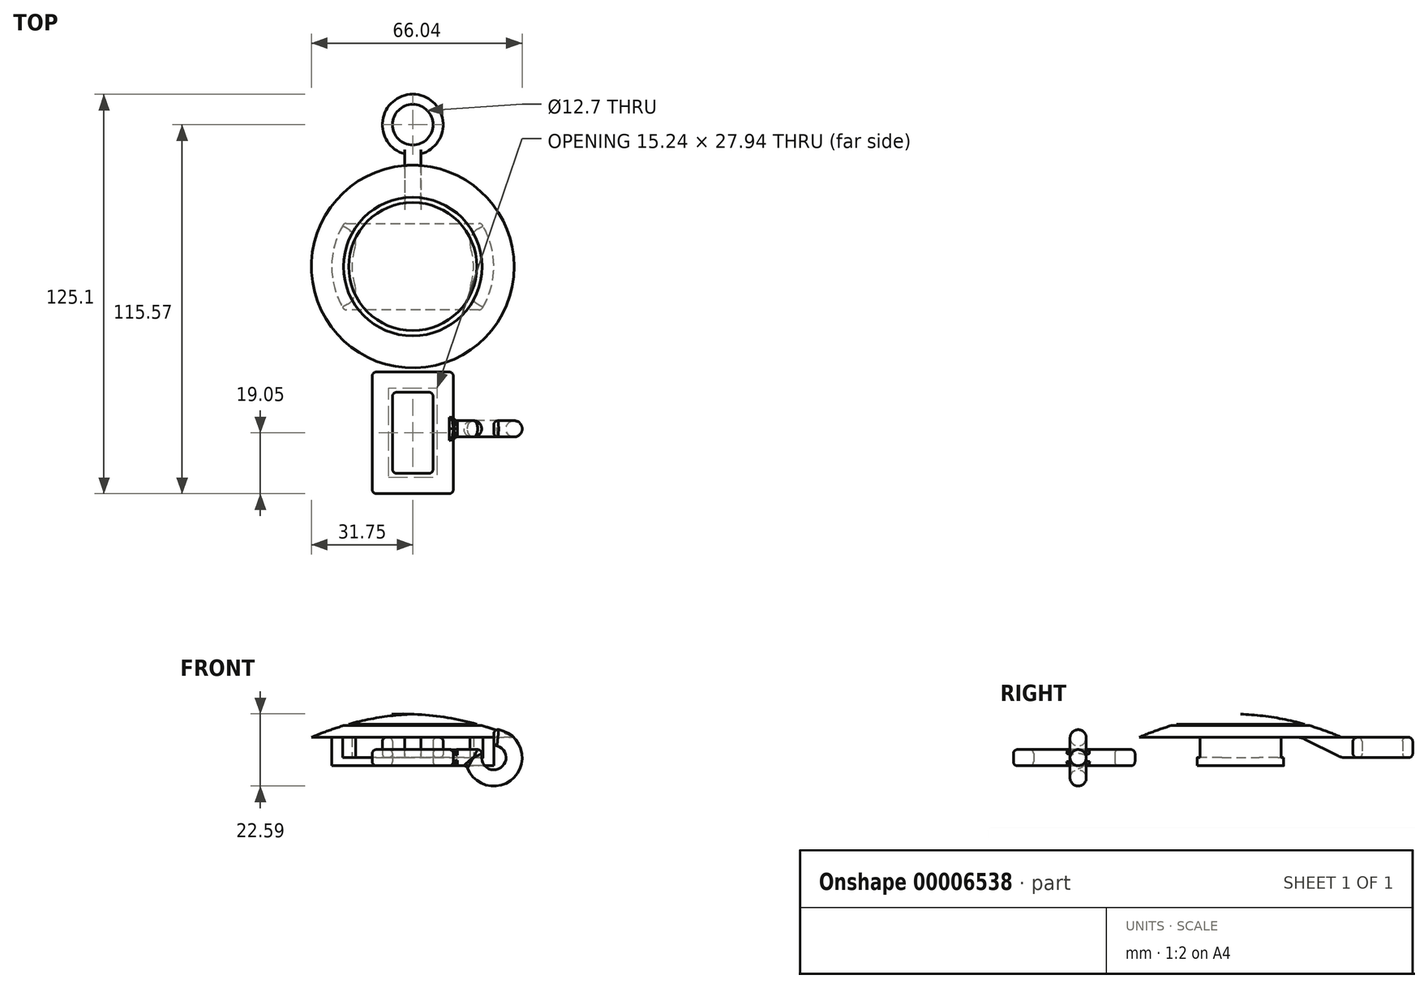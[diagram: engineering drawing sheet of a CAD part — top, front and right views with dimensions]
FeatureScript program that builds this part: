
annotation { "Feature Type Name" : "Feature", "Feature Type Description" : "" }
export const myFeature = defineFeature(function(context is Context, id is Id, definition is map)
    precondition{}
    {
        {
            var Q0;
            Q0=qCreatedBy(makeId("Top.planeOp"),FACE);
            var sketch = newSketch(context, id + "F0", { "sketchPlane" : qUnion([Q0])});
            skArc(sketch, "E0", {"start": v(-21.5, 13.54) * mm, "mid": v(-25.4, 0) * mm, "end": v(-21.5, -13.54) * mm});
            skLineSegment(sketch, "E1", {"start": v(-21.5, 13.54) * mm, "end": v(21.5, 13.54) * mm});
            skLineSegment(sketch, "E2", {"start": v(21.5, -13.54) * mm, "end": v(-21.5, -13.54) * mm});
            skArc(sketch, "E3.trimOffspring", {"start": v(21.5, -13.54) * mm, "mid": v(25.4, 0) * mm, "end": v(21.5, 13.54) * mm});
            skSolve(sketch);
        }
        {
            var Q0;
            Q0=makeQuery(id+"F0.imprint","IMPRINT",FACE,{"disambiguationData":[TD([[makeQuery(id+"F0.imprint","IMPRINT",EDGE,{"derivedFrom":sQuery(id+"F0.wireOp",EDGE,"E0")}),1.0]])]});
            extrude(context, id + "F1", {"entities" : qUnion([Q0]), "oppositeDirection" : true, "depth" : 2.54 * mm});
        }
        {
            var Q0;
            Q0=qCreatedBy(makeId("Top.planeOp"),FACE);
            var sketch = newSketch(context, id + "F2", { "sketchPlane" : qUnion([Q0])});
            skArc(sketch, "E4", {"start": v(-16.5, 9.52) * mm, "mid": v(-19.05, 0) * mm, "end": v(-16.5, -9.53) * mm});
            skArc(sketch, "E5", {"start": v(-22, 12.7) * mm, "mid": v(-25.4, 0) * mm, "end": v(-22, -12.7) * mm});
            skLineSegment(sketch, "E6", {"start": v(19.05, 0) * mm, "end": v(37.65, 0) * mm});
            skLineSegment(sketch, "E7", {"start": v(16.5, 9.53) * mm, "end": v(22, 12.7) * mm});
            skLineSegment(sketch, "E8", {"start": v(16.5, -9.53) * mm, "end": v(22, -12.7) * mm});
            skLineSegment(sketch, "E9", {"start": v(-16.5, -9.53) * mm, "end": v(-22, -12.7) * mm});
            skLineSegment(sketch, "E10", {"start": v(-19.05, 0) * mm, "end": v(-25.4, 0) * mm});
            skLineSegment(sketch, "E11", {"start": v(-16.5, 9.53) * mm, "end": v(-22, 12.7) * mm});
            skArc(sketch, "E12.trimOffspring", {"start": v(16.5, -9.53) * mm, "mid": v(19.05, 0) * mm, "end": v(16.5, 9.53) * mm});
            skArc(sketch, "E13.trimOffspring", {"start": v(22, -12.7) * mm, "mid": v(25.4, 0) * mm, "end": v(22, 12.7) * mm});
            skSolve(sketch);
        }
        {
            var Q0;
            {var subQ1=sQuery(id+"F2.wireOp",EDGE,"E10");Q0=makeQuery(id+"F2.imprint","IMPRINT",FACE,{"disambiguationData":[TD([[makeQuery(id+"F2.imprint","IMPRINT",EDGE,{"derivedFrom":subQ1}),-1.0]])]});}
            var Q1;
            {var subQ1=sQuery(id+"F2.wireOp",EDGE,"E9");Q1=makeQuery(id+"F2.imprint","IMPRINT",FACE,{"disambiguationData":[TD([[makeQuery(id+"F2.imprint","IMPRINT",EDGE,{"derivedFrom":subQ1}),-1.0]])]});}
            var Q2;
            {var subQ3=sQuery(id+"F2.wireOp",EDGE,"E8");Q2=makeQuery(id+"F2.imprint","IMPRINT",FACE,{"disambiguationData":[TD([[makeQuery(id+"F2.imprint","IMPRINT",EDGE,{"derivedFrom":subQ3}),1.0]])]});}
            var Q3;
            {var subQ3=sQuery(id+"F2.wireOp",EDGE,"E7");Q3=makeQuery(id+"F2.imprint","IMPRINT",FACE,{"disambiguationData":[TD([[makeQuery(id+"F2.imprint","IMPRINT",EDGE,{"derivedFrom":subQ3}),-1.0]])]});}
            extrude(context, id + "F3", {"entities" : qUnion([Q0, Q1, Q2, Q3]), "operationType" : NewBodyOperationType.ADD, "depth" : 6.35 * mm});
        }
        {
            var Q0;
            Q0=makeQuery(id+"F3.opExtrude","SWEPT_EDGE",EDGE,{"disambiguationData":[OSD([sQuery(id+"F2.wireOp",EDGE,"E4"),sQuery(id+"F2.wireOp",EDGE,"E9")])]});
            var Q1;
            Q1=makeQuery(id+"F3.opExtrude","SWEPT_EDGE",EDGE,{"disambiguationData":[OSD([sQuery(id+"F2.wireOp",EDGE,"E4"),sQuery(id+"F2.wireOp",EDGE,"E11")])]});
            var Q2;
            Q2=makeQuery(id+"F3.opExtrude","SWEPT_EDGE",EDGE,{"disambiguationData":[OSD([sQuery(id+"F2.wireOp",EDGE,"E8"),sQuery(id+"F2.wireOp",EDGE,"E12.trimOffspring")])]});
            var Q3;
            Q3=makeQuery(id+"F3.opExtrude","SWEPT_EDGE",EDGE,{"disambiguationData":[OSD([sQuery(id+"F2.wireOp",EDGE,"E7"),sQuery(id+"F2.wireOp",EDGE,"E12.trimOffspring")])]});
            fillet(context, id + "F4", {"entities" : qUnion([Q0, Q1, Q2, Q3]), "radius" : 5.08 * mm, "tangentPropagation" : true, "allowEdgeOverflow" : false});
        }
        {
            var Q0;
            Q0=makeQuery(id+"F1.opExtrude","SWEPT_EDGE",EDGE,{"disambiguationData":[OSD([sQuery(id+"F0.wireOp",EDGE,"E0"),sQuery(id+"F0.wireOp",EDGE,"E1")])]});
            var Q1;
            Q1=makeQuery(id+"F1.opExtrude","SWEPT_EDGE",EDGE,{"disambiguationData":[OSD([sQuery(id+"F0.wireOp",EDGE,"E1"),sQuery(id+"F0.wireOp",EDGE,"E3.trimOffspring")])]});
            var Q2;
            Q2=makeQuery(id+"F1.opExtrude","SWEPT_EDGE",EDGE,{"disambiguationData":[OSD([sQuery(id+"F0.wireOp",EDGE,"E2"),sQuery(id+"F0.wireOp",EDGE,"E3.trimOffspring")])]});
            var Q3;
            Q3=makeQuery(id+"F1.opExtrude","SWEPT_EDGE",EDGE,{"disambiguationData":[OSD([sQuery(id+"F0.wireOp",EDGE,"E0"),sQuery(id+"F0.wireOp",EDGE,"E2")])]});
            fillet(context, id + "F5", {"entities" : qUnion([Q0, Q1, Q2, Q3]), "radius" : 1.27 * mm, "tangentPropagation" : true, "allowEdgeOverflow" : false});
        }
        {
            var Q0;
            Q0=qCreatedBy(makeId("Front.planeOp"),FACE);
            var sketch = newSketch(context, id + "F6", { "sketchPlane" : qUnion([Q0])});
            skLineSegment(sketch, "E14.0", {"start": v(-25.4, 6.35) * mm, "end": v(-22, 6.35) * mm});
            skLineSegment(sketch, "E15.1", {"start": v(22, 6.35) * mm, "end": v(25.4, 6.35) * mm});
            skLineSegment(sketch, "E16", {"start": v(-25.4, 6.35) * mm, "end": v(25.4, 6.35) * mm});
            skLineSegment(sketch, "E17", {"start": v(0, 6.35) * mm, "end": v(0, 13.64) * mm});
            skPoint(sketch, "E17.endSnap0", {"position": v(0, 6.35) * mm});
            skLineSegment(sketch, "E18", {"start": v(0, 6.35) * mm, "end": v(31.75, 6.35) * mm});
            skPoint(sketch, "E18.endSnap0", {"position": v(23.7, 6.35) * mm});
            skArc(sketch, "E19", {"start": v(31.75, 6.35) * mm, "mid": v(16.22, 11.5) * mm, "end": v(0, 13.64) * mm});
            skSolve(sketch);
        }
        {
            var Q0;
            {var subQ2=sQuery(id+"F6.wireOp",EDGE,"E17");Q0=makeQuery(id+"F6.imprint","IMPRINT",FACE,{"disambiguationData":[TD([[makeQuery(id+"F6.imprint","IMPRINT",EDGE,{"derivedFrom":subQ2}),-1.0]])]});}
            var Q1;
            Q1=sQuery(id+"F6.wireOp",EDGE,"E17");
            revolve(context, id + "F7", {"operationType" : NewBodyOperationType.ADD, "entities" : qUnion([Q0]), "axis" : qUnion([Q1]), "revolveType" : RevolveType.FULL});
        }
        {
            var Q0;
            Q0=qCreatedBy(makeId("Front.planeOp"),FACE);
            var sketch = newSketch(context, id + "F8", { "sketchPlane" : qUnion([Q0])});
            skLineSegment(sketch, "E20", {"start": v(20.07, 10.74) * mm, "end": v(20.07, 10.04) * mm});
            skLineSegment(sketch, "E21", {"start": v(20.07, 10.04) * mm, "end": v(22.4, 10.04) * mm});
            skLineSegment(sketch, "E22", {"start": v(22.4, 10.04) * mm, "end": v(20.07, 10.74) * mm});
            skLineSegment(sketch, "E23", {"start": v(0, 11.08) * mm, "end": v(0, 16.1) * mm});
            skSolve(sketch);
        }
        {
            var Q0;
            Q0=makeQuery(id+"F8.imprint","IMPRINT",FACE,{"disambiguationData":[TD([[makeQuery(id+"F8.imprint","IMPRINT",EDGE,{"derivedFrom":sQuery(id+"F8.wireOp",EDGE,"E20")}),1.0]])]});
            var Q1;
            Q1=sQuery(id+"F8.wireOp",EDGE,"E23");
            revolve(context, id + "F9", {"operationType" : NewBodyOperationType.REMOVE, "entities" : qUnion([Q0]), "axis" : qUnion([Q1]), "revolveType" : RevolveType.FULL, "oppositeDirection" : true});
        }
        {
            var Q0;
            Q0=qCreatedBy(makeId("Top.planeOp"),FACE);
            var sketch = newSketch(context, id + "F10", { "sketchPlane" : qUnion([Q0])});
            skArc(sketch, "E24.1.0", {"start": v(2.54, 35.27) * mm, "mid": v(0, 53.98) * mm, "end": v(-2.54, 35.27) * mm});
            skCircle(sketch, "E24.1.1", {"center": v(0, 44.45) * mm, "radius": 6.35 * mm});
            skLineSegment(sketch, "E24.1.2", {"start": v(-2.54, 35.27) * mm, "end": v(-2.54, 19.05) * mm});
            skLineSegment(sketch, "E24.1.3", {"start": v(2.54, 35.27) * mm, "end": v(2.54, 19.05) * mm});
            skLineSegment(sketch, "E24.1.4", {"start": v(2.54, 19.05) * mm, "end": v(-2.54, 19.05) * mm});
            skPoint(sketch, "E24.center", {"position": v(0, 0) * mm});
            skLineSegment(sketch, "E24.anchor2", {"start": v(0, 0) * mm, "end": v(0, 44.45) * mm, "construction": true});
            skPoint(sketch, "E25.orphan", {"position": v(-19.05, 2.54) * mm});
            skPoint(sketch, "E24.anchor1.end.orphan", {"position": v(-44.45, 0) * mm});
            skSolve(sketch);
        }
        {
            var Q0;
            Q0=makeQuery(id+"F10.imprint","IMPRINT",FACE,{"disambiguationData":[TD([[makeQuery(id+"F10.imprint","IMPRINT",EDGE,{"derivedFrom":sQuery(id+"F10.wireOp",EDGE,"E24.1.0")}),1.0]])]});
            extrude(context, id + "F11", {"entities" : qUnion([Q0]), "operationType" : NewBodyOperationType.ADD, "depth" : 6.35 * mm});
        }
        {
            var Q0;
            Q0=makeQuery(id+"F11.opExtrude","CAP_EDGE",EDGE,{"disambiguationData":[OSD([sQuery(id+"F10.wireOp",EDGE,"E24.1.4")])],"isStart":true});
            chamfer(context, id + "F12", {"entities" : qUnion([Q0]), "chamferType" : ChamferType.TWO_OFFSETS, "width1" : 12.7 * mm, "oppositeDirection" : false, "width2" : 6.35 * mm, "tangentPropagation" : true});
        }
        {
            var Q0;
            Q0=makeQuery(id+"F11.opExtrude","CAP_EDGE",EDGE,{"disambiguationData":[OSD([sQuery(id+"F10.wireOp",EDGE,"E24.1.1")])],"isStart":false});
            var Q1;
            Q1=makeQuery(id+"F11.opExtrude","CAP_EDGE",EDGE,{"disambiguationData":[OSD([sQuery(id+"F10.wireOp",EDGE,"E24.1.0")])],"isStart":false});
            var Q2;
            Q2=makeQuery(id+"F11.opExtrude","CAP_EDGE",EDGE,{"disambiguationData":[OSD([sQuery(id+"F10.wireOp",EDGE,"E24.1.0")])],"isStart":true});
            var Q3;
            Q3=makeQuery(id+"F11.opExtrude","CAP_EDGE",EDGE,{"disambiguationData":[OSD([sQuery(id+"F10.wireOp",EDGE,"E24.1.1")])],"isStart":true});
            fillet(context, id + "F13", {"entities" : qUnion([Q0, Q1, Q2, Q3]), "radius" : 1.27 * mm, "tangentPropagation" : true, "allowEdgeOverflow" : false});
        }
        {
            var Q0;
            Q0=makeQuery(id+"F12.opChamfer","BLEND_EDGE",EDGE,{"blendedFrom":[makeQuery(id+"F11.opExtrude","CAP_EDGE",EDGE,{"disambiguationData":[OSD([sQuery(id+"F10.wireOp",EDGE,"E24.1.4")])],"isStart":true}),makeQuery(id+"F7.opRevolve","SWEPT_FACE",FACE,{"disambiguationData":[OSD([sQuery(id+"F6.wireOp",EDGE,"E18")])]})],"blendedInto":[makeQuery(id+"F7.opRevolve","SWEPT_FACE",FACE,{"disambiguationData":[OSD([sQuery(id+"F6.wireOp",EDGE,"E18")])]})]});
            var Q1;
            {var subQ0=sQuery(id+"F10.wireOp",EDGE,"E24.1.4");Q1=makeQuery(id+"F12.opChamfer","BLEND_EDGE",EDGE,{"blendedFrom":[makeQuery(id+"F11.opExtrude","CAP_EDGE",EDGE,{"disambiguationData":[OSD([subQ0])],"isStart":true}),makeQuery(id+"F11.opExtrude","CAP_FACE",FACE,{"disambiguationData":[OSD([sQuery(id+"F10.wireOp",EDGE,"E24.1.0"),sQuery(id+"F10.wireOp",EDGE,"E24.1.1"),sQuery(id+"F10.wireOp",EDGE,"E24.1.2"),sQuery(id+"F10.wireOp",EDGE,"E24.1.3"),subQ0])],"isStart":true})],"blendedInto":[makeQuery(id+"F11.opExtrude","CAP_FACE",FACE,{"disambiguationData":[OSD([sQuery(id+"F10.wireOp",EDGE,"E24.1.0"),sQuery(id+"F10.wireOp",EDGE,"E24.1.1"),sQuery(id+"F10.wireOp",EDGE,"E24.1.2"),sQuery(id+"F10.wireOp",EDGE,"E24.1.3"),subQ0])],"isStart":true})]});}
            fillet(context, id + "F14", {"entities" : qUnion([Q0, Q1]), "radius" : 5.08 * mm, "tangentPropagation" : true, "allowEdgeOverflow" : false});
        }
        {
            var Q0;
            Q0=qCreatedBy(makeId("Top.planeOp"),FACE);
            var sketch = newSketch(context, id + "F15", { "sketchPlane" : qUnion([Q0])});
            skLineSegment(sketch, "E26.bottom", {"start": v(-12.7, -71.12) * mm, "end": v(12.7, -71.12) * mm});
            skLineSegment(sketch, "E26.top", {"start": v(-12.7, -33.02) * mm, "end": v(12.7, -33.02) * mm});
            skLineSegment(sketch, "E26.left", {"start": v(-12.7, -71.12) * mm, "end": v(-12.7, -33.02) * mm});
            skLineSegment(sketch, "E26.right", {"start": v(12.7, -71.12) * mm, "end": v(12.7, -33.02) * mm});
            skLineSegment(sketch, "E27.0", {"start": v(-6.35, -39.37) * mm, "end": v(6.35, -39.37) * mm});
            skLineSegment(sketch, "E27.1", {"start": v(-6.35, -64.77) * mm, "end": v(-6.35, -39.37) * mm});
            skLineSegment(sketch, "E27.2", {"start": v(-6.35, -64.77) * mm, "end": v(6.35, -64.77) * mm});
            skLineSegment(sketch, "E27.3", {"start": v(6.35, -64.77) * mm, "end": v(6.35, -39.37) * mm});
            skSolve(sketch);
        }
        {
            var Q0;
            Q0=makeQuery(id+"F15.imprint","IMPRINT",FACE,{"disambiguationData":[TD([[makeQuery(id+"F15.imprint","IMPRINT",EDGE,{"derivedFrom":sQuery(id+"F15.wireOp",EDGE,"E26.bottom")}),1.0]])]});
            extrude(context, id + "F16", {"entities" : qUnion([Q0]), "endBound" : BoundingType.SYMMETRIC, "depth" : 5.08 * mm});
        }
        {
            var Q0;
            Q0=qCreatedBy(makeId("Front.planeOp"),FACE);
            cPlane(context, id + "F17", {"entities" : qUnion([Q0]), "cplaneType" : CPlaneType.OFFSET, "offset" : 50.8 * mm, "width" : 152.4 * mm, "height" : 152.4 * mm});
        }
        {
            var Q0;
            Q0=qCreatedBy(id+"F17.planeOp",FACE);
            var sketch = newSketch(context, id + "F18", { "sketchPlane" : qUnion([Q0])});
            skLineSegment(sketch, "E28.0", {"start": v(12.7, 2.54) * mm, "end": v(12.7, -2.54) * mm});
            skLineSegment(sketch, "E29", {"start": v(12.7, 0) * mm, "end": v(19.05, 0) * mm});
            skPoint(sketch, "E29.endSnap0", {"position": v(12.7, 0) * mm});
            skArc(sketch, "E30", {"start": v(19.05, 0) * mm, "mid": v(29.9, -4.5) * mm, "end": v(25.4, 6.35) * mm});
            skSolve(sketch);
        }
        {
            var Q0;
            Q0=makeQuery(id+"F16.opExtrude","SWEPT_FACE",FACE,{"disambiguationData":[OSD([sQuery(id+"F15.wireOp",EDGE,"E26.right")])]});
            var sketch = newSketch(context, id + "F19", { "sketchPlane" : qUnion([Q0])});
            skLineSegment(sketch, "E31.0", {"start": v(-71.12, 2.54) * mm, "end": v(-33.02, 2.54) * mm});
            skLineSegment(sketch, "E31.1", {"start": v(-71.12, -2.54) * mm, "end": v(-33.02, -2.54) * mm});
            skLineSegment(sketch, "E32", {"start": v(-50.82, 2.54) * mm, "end": v(-50.82, -2.54) * mm});
            skCircle(sketch, "E33", {"center": v(-50.82, 0) * mm, "radius": 2.54 * mm});
            skSolve(sketch);
        }
        {
            var Q0;
            {var subQ1=sQuery(id+"F19.wireOp",EDGE,"E32");Q0=makeQuery(id+"F19.imprint","IMPRINT",FACE,{"disambiguationData":[TD([[makeQuery(id+"F19.imprint","IMPRINT",EDGE,{"derivedFrom":subQ1}),-1.0]])]});}
            var Q1;
            {var subQ1=sQuery(id+"F19.wireOp",EDGE,"E32");Q1=makeQuery(id+"F19.imprint","IMPRINT",FACE,{"disambiguationData":[TD([[makeQuery(id+"F19.imprint","IMPRINT",EDGE,{"derivedFrom":subQ1}),1.0]])]});}
            var Q2;
            Q2=sQuery(id+"F18.wireOp",EDGE,"E29");
            var Q3;
            Q3=sQuery(id+"F18.wireOp",EDGE,"E30");
            sweep(context, id + "F20", {"operationType" : NewBodyOperationType.ADD, "profiles" : qUnion([Q0, Q1]), "path" : qUnion([Q2, Q3])});
        }
        {
            var Q0;
            Q0=makeQuery(id+"F20.opSweep","MID_CAP_EDGE",EDGE,{"disambiguationData":[OSD([sQuery(id+"F18.wireOp",VERTEX,"E30.start"),sQuery(id+"F19.wireOp",EDGE,"E33")]),OD(1.0)],"capPos":1.0});
            var Q1;
            Q1=makeQuery(id+"F20.opSweep","MID_CAP_EDGE",EDGE,{"disambiguationData":[OSD([sQuery(id+"F18.wireOp",VERTEX,"E30.start"),sQuery(id+"F19.wireOp",EDGE,"E33")]),OD(0.0)],"capPos":1.0});
            var Q2;
            Q2=makeQuery(id+"F20.opSweep","CAP_EDGE",EDGE,{"disambiguationData":[OSD([sQuery(id+"F18.wireOp",VERTEX,"E30.end"),sQuery(id+"F19.wireOp",EDGE,"E33")])],"isStart":false});
            var Q3;
            {var subQ0=sQuery(id+"F15.wireOp",EDGE,"E26.right");var subQ1=sQuery(id+"F15.wireOp",EDGE,"E26.bottom");Q3=makeQuery(id+"F20.boolean.opBoolean","SPLIT",EDGE,{"disambiguationData":[TD([makeQuery(id+"F16.opExtrude","SWEPT_FACE",FACE,{"disambiguationData":[OSD([subQ1])]})])],"derivedFrom":makeQuery(id+"F16.opExtrude","CAP_EDGE",EDGE,{"disambiguationData":[OSD([subQ0])],"isStart":false})});}
            var Q4;
            {var subQ0=sQuery(id+"F15.wireOp",EDGE,"E26.right");var subQ1=sQuery(id+"F15.wireOp",EDGE,"E26.top");Q4=makeQuery(id+"F20.boolean.opBoolean","SPLIT",EDGE,{"disambiguationData":[TD([makeQuery(id+"F16.opExtrude","SWEPT_FACE",FACE,{"disambiguationData":[OSD([subQ1])]})])],"derivedFrom":makeQuery(id+"F16.opExtrude","CAP_EDGE",EDGE,{"disambiguationData":[OSD([subQ0])],"isStart":false})});}
            var Q5;
            Q5=makeQuery(id+"F20.boolean.opBoolean","SPLIT",EDGE,{"disambiguationData":[OD(0.0)],"derivedFrom":makeQuery(id+"F20.opSweep","CAP_EDGE",EDGE,{"disambiguationData":[OSD([sQuery(id+"F18.wireOp",VERTEX,"E29.start"),sQuery(id+"F19.wireOp",EDGE,"E33")])],"isStart":true})});
            var Q6;
            {var subQ0=sQuery(id+"F15.wireOp",EDGE,"E26.right");var subQ1=sQuery(id+"F15.wireOp",EDGE,"E26.bottom");Q6=makeQuery(id+"F20.boolean.opBoolean","SPLIT",EDGE,{"disambiguationData":[TD([makeQuery(id+"F16.opExtrude","SWEPT_FACE",FACE,{"disambiguationData":[OSD([subQ1])]})])],"derivedFrom":makeQuery(id+"F16.opExtrude","CAP_EDGE",EDGE,{"disambiguationData":[OSD([subQ0])],"isStart":true})});}
            var Q7;
            {var subQ0=sQuery(id+"F15.wireOp",EDGE,"E26.right");var subQ1=sQuery(id+"F15.wireOp",EDGE,"E26.top");Q7=makeQuery(id+"F20.boolean.opBoolean","SPLIT",EDGE,{"disambiguationData":[TD([makeQuery(id+"F16.opExtrude","SWEPT_FACE",FACE,{"disambiguationData":[OSD([subQ1])]})])],"derivedFrom":makeQuery(id+"F16.opExtrude","CAP_EDGE",EDGE,{"disambiguationData":[OSD([subQ0])],"isStart":true})});}
            var Q8;
            Q8=makeQuery(id+"F20.boolean.opBoolean","SPLIT",EDGE,{"disambiguationData":[OD(1.0)],"derivedFrom":makeQuery(id+"F20.opSweep","CAP_EDGE",EDGE,{"disambiguationData":[OSD([sQuery(id+"F18.wireOp",VERTEX,"E29.start"),sQuery(id+"F19.wireOp",EDGE,"E33")])],"isStart":true})});
            var Q9;
            Q9=makeQuery(id+"F16.opExtrude","CAP_EDGE",EDGE,{"disambiguationData":[OSD([sQuery(id+"F15.wireOp",EDGE,"E27.3")])],"isStart":true});
            var Q10;
            Q10=makeQuery(id+"F16.opExtrude","CAP_EDGE",EDGE,{"disambiguationData":[OSD([sQuery(id+"F15.wireOp",EDGE,"E27.2")])],"isStart":true});
            var Q11;
            Q11=makeQuery(id+"F16.opExtrude","CAP_EDGE",EDGE,{"disambiguationData":[OSD([sQuery(id+"F15.wireOp",EDGE,"E27.1")])],"isStart":true});
            var Q12;
            Q12=makeQuery(id+"F16.opExtrude","CAP_EDGE",EDGE,{"disambiguationData":[OSD([sQuery(id+"F15.wireOp",EDGE,"E27.0")])],"isStart":true});
            var Q13;
            Q13=makeQuery(id+"F16.opExtrude","CAP_EDGE",EDGE,{"disambiguationData":[OSD([sQuery(id+"F15.wireOp",EDGE,"E27.2")])],"isStart":false});
            var Q14;
            Q14=makeQuery(id+"F16.opExtrude","CAP_EDGE",EDGE,{"disambiguationData":[OSD([sQuery(id+"F15.wireOp",EDGE,"E27.1")])],"isStart":false});
            var Q15;
            Q15=makeQuery(id+"F16.opExtrude","CAP_EDGE",EDGE,{"disambiguationData":[OSD([sQuery(id+"F15.wireOp",EDGE,"E27.3")])],"isStart":false});
            var Q16;
            Q16=makeQuery(id+"F16.opExtrude","CAP_EDGE",EDGE,{"disambiguationData":[OSD([sQuery(id+"F15.wireOp",EDGE,"E27.0")])],"isStart":false});
            var Q17;
            Q17=makeQuery(id+"F16.opExtrude","CAP_EDGE",EDGE,{"disambiguationData":[OSD([sQuery(id+"F15.wireOp",EDGE,"E26.left")])],"isStart":true});
            var Q18;
            Q18=makeQuery(id+"F16.opExtrude","CAP_EDGE",EDGE,{"disambiguationData":[OSD([sQuery(id+"F15.wireOp",EDGE,"E26.top")])],"isStart":true});
            var Q19;
            Q19=makeQuery(id+"F16.opExtrude","CAP_EDGE",EDGE,{"disambiguationData":[OSD([sQuery(id+"F15.wireOp",EDGE,"E26.top")])],"isStart":false});
            var Q20;
            Q20=makeQuery(id+"F16.opExtrude","CAP_EDGE",EDGE,{"disambiguationData":[OSD([sQuery(id+"F15.wireOp",EDGE,"E26.left")])],"isStart":false});
            var Q21;
            Q21=makeQuery(id+"F16.opExtrude","CAP_EDGE",EDGE,{"disambiguationData":[OSD([sQuery(id+"F15.wireOp",EDGE,"E26.bottom")])],"isStart":true});
            var Q22;
            Q22=makeQuery(id+"F16.opExtrude","CAP_EDGE",EDGE,{"disambiguationData":[OSD([sQuery(id+"F15.wireOp",EDGE,"E26.bottom")])],"isStart":false});
            var Q23;
            {var subQ0=sQuery(id+"F15.wireOp",EDGE,"E26.right");var subQ1=makeQuery(id+"F16.opExtrude","SWEPT_FACE",FACE,{"disambiguationData":[OSD([subQ0])]});var subQ2=sQuery(id+"F15.wireOp",EDGE,"E26.bottom");Q23=makeQuery(id+"F20.boolean.opBoolean","SPLIT",FACE,{"disambiguationData":[TD([makeQuery(id+"F16.opExtrude","SWEPT_FACE",FACE,{"disambiguationData":[OSD([subQ2])]})])],"derivedFrom":subQ1});}
            var Q24;
            Q24=makeQuery(id+"F16.opExtrude","SWEPT_EDGE",EDGE,{"disambiguationData":[OSD([sQuery(id+"F15.wireOp",EDGE,"E26.bottom"),sQuery(id+"F15.wireOp",EDGE,"E26.left")])]});
            var Q25;
            Q25=makeQuery(id+"F16.opExtrude","SWEPT_EDGE",EDGE,{"disambiguationData":[OSD([sQuery(id+"F15.wireOp",EDGE,"E26.top"),sQuery(id+"F15.wireOp",EDGE,"E26.right")])]});
            var Q26;
            Q26=makeQuery(id+"F16.opExtrude","SWEPT_EDGE",EDGE,{"disambiguationData":[OSD([sQuery(id+"F15.wireOp",EDGE,"E26.top"),sQuery(id+"F15.wireOp",EDGE,"E26.left")])]});
            var Q27;
            Q27=makeQuery(id+"F16.opExtrude","SWEPT_EDGE",EDGE,{"disambiguationData":[OSD([sQuery(id+"F15.wireOp",EDGE,"E27.1"),sQuery(id+"F15.wireOp",EDGE,"E27.2")])]});
            var Q28;
            Q28=makeQuery(id+"F16.opExtrude","SWEPT_EDGE",EDGE,{"disambiguationData":[OSD([sQuery(id+"F15.wireOp",EDGE,"E27.2"),sQuery(id+"F15.wireOp",EDGE,"E27.3")])]});
            var Q29;
            Q29=makeQuery(id+"F16.opExtrude","SWEPT_EDGE",EDGE,{"disambiguationData":[OSD([sQuery(id+"F15.wireOp",EDGE,"E27.0"),sQuery(id+"F15.wireOp",EDGE,"E27.1")])]});
            var Q30;
            Q30=makeQuery(id+"F16.opExtrude","SWEPT_EDGE",EDGE,{"disambiguationData":[OSD([sQuery(id+"F15.wireOp",EDGE,"E27.0"),sQuery(id+"F15.wireOp",EDGE,"E27.3")])]});
            fillet(context, id + "F21", {"entities" : qUnion([Q0, Q1, Q2, Q3, Q4, Q5, Q6, Q7, Q8, Q9, Q10, Q11, Q12, Q13, Q14, Q15, Q16, Q17, Q18, Q19, Q20, Q21, Q22, Q23, Q24, Q25, Q26, Q27, Q28, Q29, Q30]), "radius" : 1.27 * mm, "tangentPropagation" : true, "allowEdgeOverflow" : false});
        }
    });
